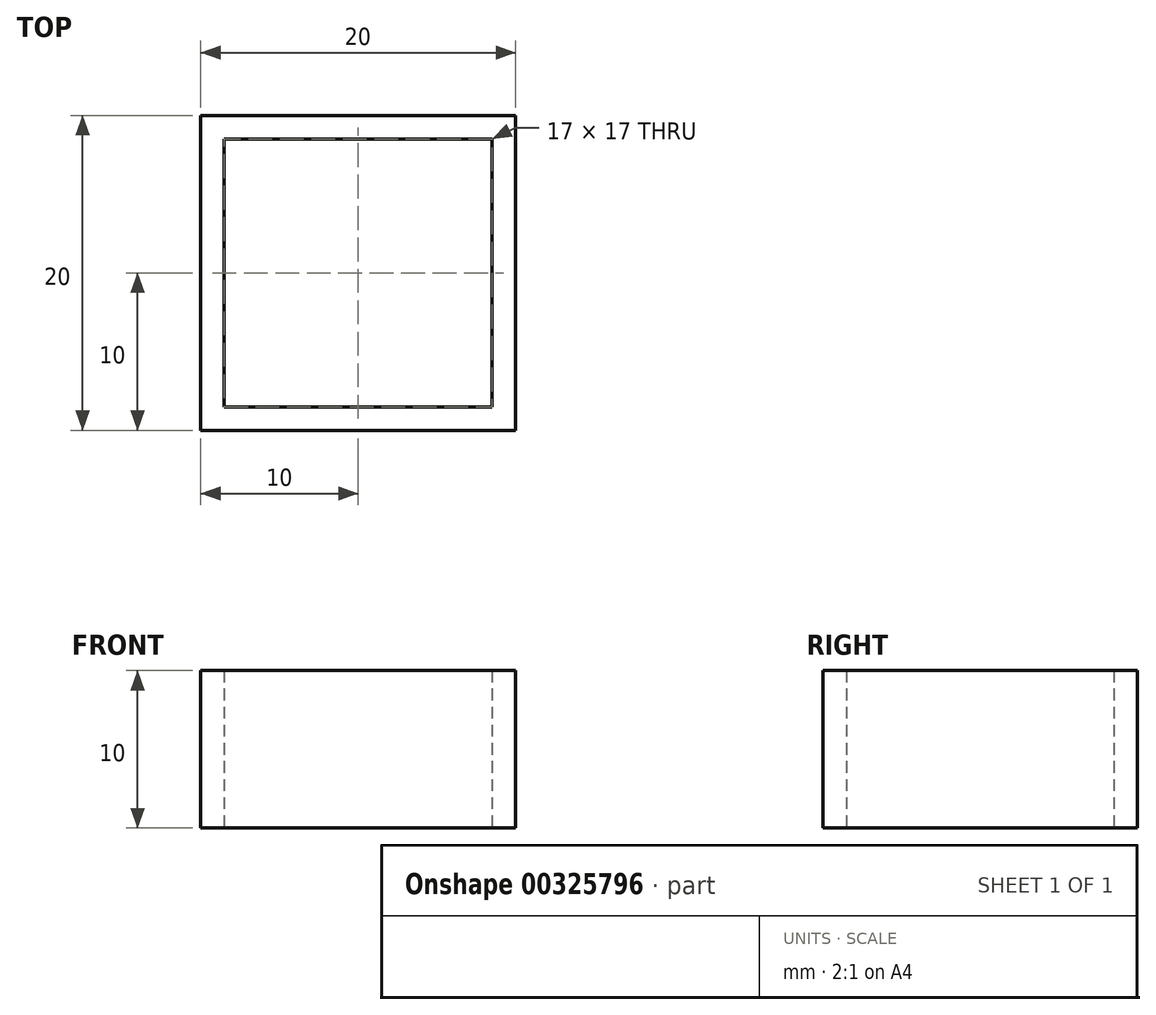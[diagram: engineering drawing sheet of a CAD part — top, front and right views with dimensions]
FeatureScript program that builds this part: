
annotation { "Feature Type Name" : "Feature", "Feature Type Description" : "" }
export const myFeature = defineFeature(function(context is Context, id is Id, definition is map)
    precondition{}
    {
        {
            var Q0;
            Q0=qCreatedBy(makeId("Top.planeOp"),FACE);
            var sketch = newSketch(context, id + "F0", { "sketchPlane" : qUnion([Q0])});
            skLineSegment(sketch, "E0.bottom", {"start": v(8.5, -8.5) * mm, "end": v(-8.5, -8.5) * mm});
            skLineSegment(sketch, "E0.top", {"start": v(8.5, 8.5) * mm, "end": v(-8.5, 8.5) * mm});
            skLineSegment(sketch, "E0.left", {"start": v(8.5, -8.5) * mm, "end": v(8.5, 8.5) * mm});
            skLineSegment(sketch, "E0.right", {"start": v(-8.5, -8.5) * mm, "end": v(-8.5, 8.5) * mm});
            skPoint(sketch, "E0.middle", {"position": v(0, 0) * mm});
            skLineSegment(sketch, "E1.bottom", {"start": v(10, -10) * mm, "end": v(-10, -10) * mm});
            skLineSegment(sketch, "E1.top", {"start": v(10, 10) * mm, "end": v(-10, 10) * mm});
            skLineSegment(sketch, "E1.left", {"start": v(10, -10) * mm, "end": v(10, 10) * mm});
            skLineSegment(sketch, "E1.right", {"start": v(-10, -10) * mm, "end": v(-10, 10) * mm});
            skSolve(sketch);
        }
        {
            var Q0;
            Q0=makeQuery(id+"F0.imprint","IMPRINT",FACE,{"disambiguationData":[TD([[makeQuery(id+"F0.imprint","IMPRINT",EDGE,{"derivedFrom":sQuery(id+"F0.wireOp",EDGE,"E0.bottom")}),1.0]])]});
            extrude(context, id + "F1", {"entities" : qUnion([Q0]), "depth" : 10 * mm});
        }
    });
